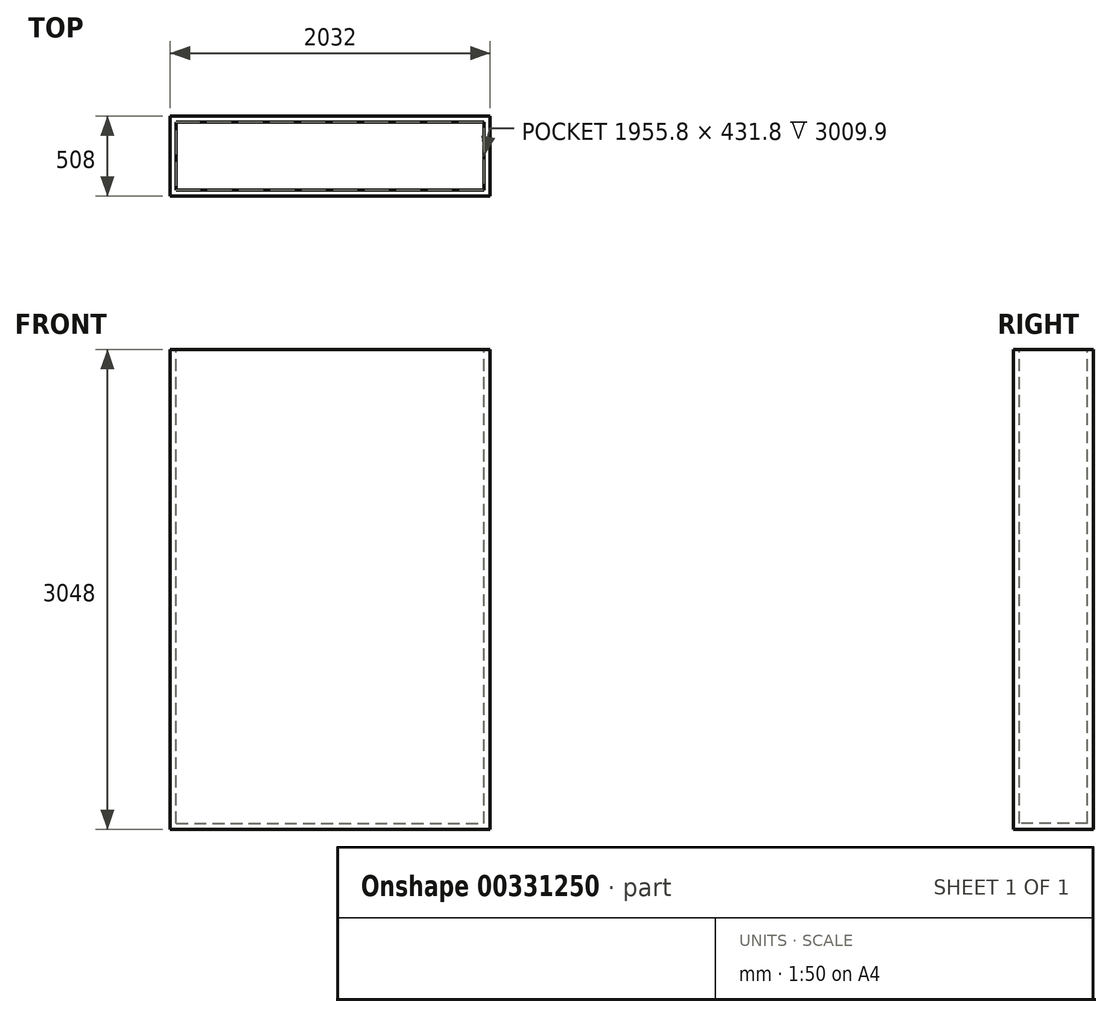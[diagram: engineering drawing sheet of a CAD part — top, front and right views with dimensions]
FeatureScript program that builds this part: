
annotation { "Feature Type Name" : "Feature", "Feature Type Description" : "" }
export const myFeature = defineFeature(function(context is Context, id is Id, definition is map)
    precondition{}
    {
        {
            var Q0;
            Q0=qCreatedBy(makeId("Front.planeOp"),FACE);
            var sketch = newSketch(context, id + "F0", { "sketchPlane" : qUnion([Q0])});
            skLineSegment(sketch, "E0.bottom", {"start": v(0, 0) * mm, "end": v(2032, 0) * mm});
            skLineSegment(sketch, "E0.top", {"start": v(0, 3048) * mm, "end": v(2032, 3048) * mm});
            skLineSegment(sketch, "E0.left", {"start": v(0, 0) * mm, "end": v(0, 3048) * mm});
            skLineSegment(sketch, "E0.right", {"start": v(2032, 0) * mm, "end": v(2032, 3048) * mm});
            skSolve(sketch);
        }
        {
            var Q0;
            Q0=makeQuery(id+"F0.imprint","IMPRINT",FACE,{"disambiguationData":[TD([[makeQuery(id+"F0.imprint","IMPRINT",EDGE,{"derivedFrom":sQuery(id+"F0.wireOp",EDGE,"E0.bottom")}),1.0]])]});
            extrude(context, id + "F1", {"entities" : qUnion([Q0]), "oppositeDirection" : true, "depth" : 508 * mm});
        }
        {
            var Q0;
            Q0=makeQuery(id+"F1.opExtrude","SWEPT_FACE",FACE,{"disambiguationData":[OSD([sQuery(id+"F0.wireOp",EDGE,"E0.top")])]});
            var sketch = newSketch(context, id + "F2", { "sketchPlane" : qUnion([Q0])});
            skLineSegment(sketch, "E1.0", {"start": v(38.1, 469.9) * mm, "end": v(1993.9, 469.9) * mm});
            skLineSegment(sketch, "E1.1", {"start": v(38.1, 469.9) * mm, "end": v(38.1, 38.1) * mm});
            skLineSegment(sketch, "E1.2", {"start": v(38.1, 38.1) * mm, "end": v(1993.9, 38.1) * mm});
            skLineSegment(sketch, "E1.3", {"start": v(1993.9, 469.9) * mm, "end": v(1993.9, 38.1) * mm});
            skSolve(sketch);
        }
        {
            var Q0;
            Q0=makeQuery(id+"F2.imprint","IMPRINT",FACE,{"disambiguationData":[TD([[makeQuery(id+"F2.imprint","IMPRINT",EDGE,{"derivedFrom":sQuery(id+"F2.wireOp",EDGE,"E1.0")}),-1.0]])]});
            extrude(context, id + "F3", {"entities" : qUnion([Q0]), "operationType" : NewBodyOperationType.REMOVE, "oppositeDirection" : true, "depth" : 3009.9 * mm});
        }
    });
